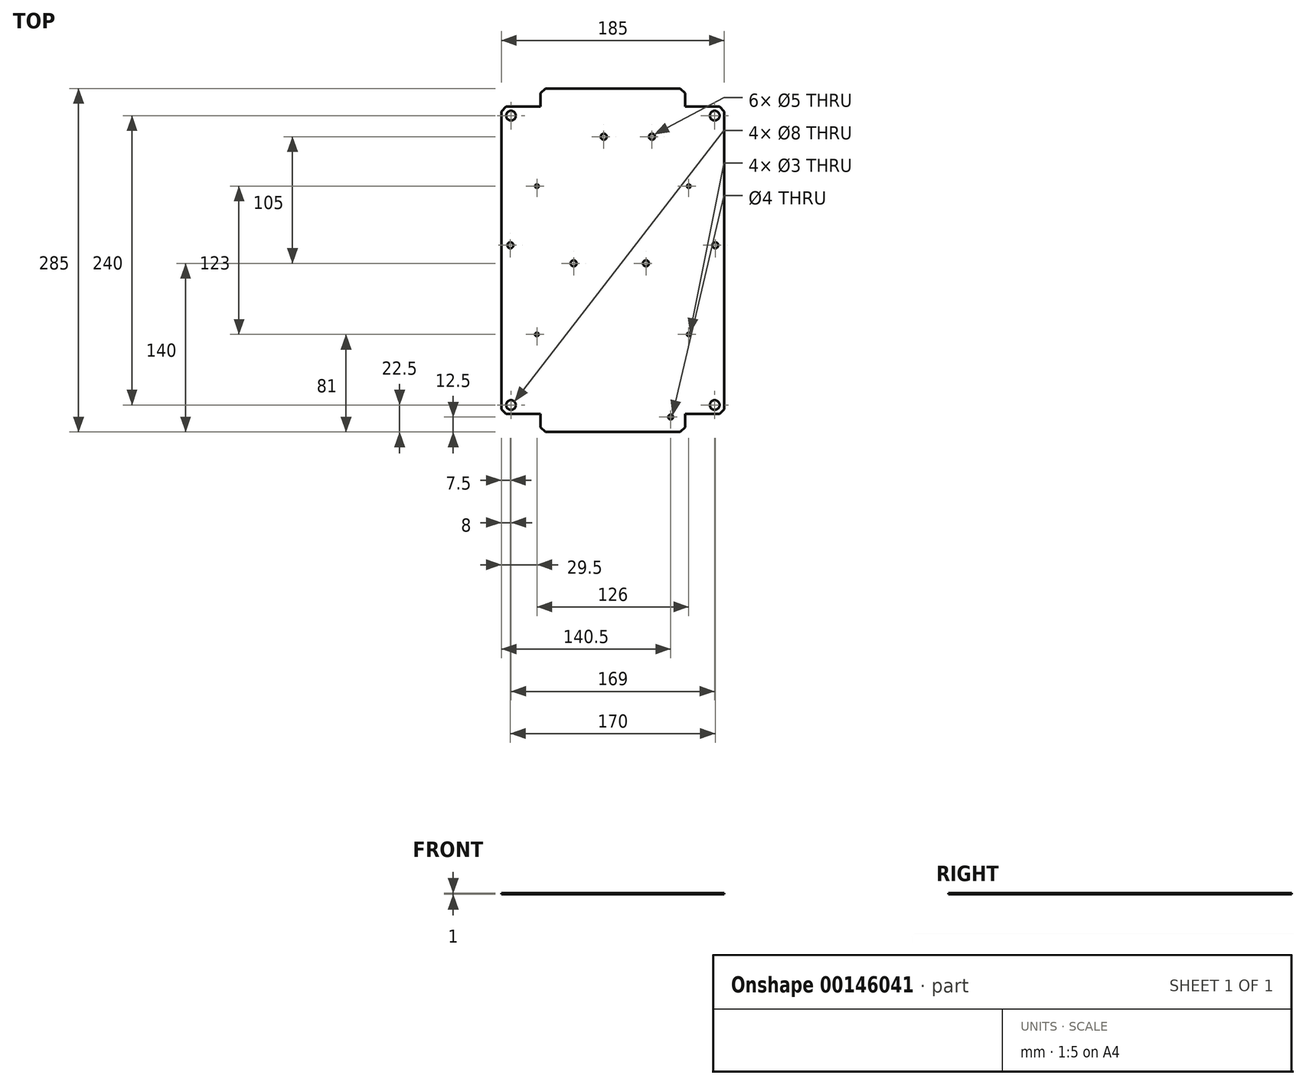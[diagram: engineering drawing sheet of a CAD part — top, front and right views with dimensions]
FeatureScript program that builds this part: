
annotation { "Feature Type Name" : "Feature", "Feature Type Description" : "" }
export const myFeature = defineFeature(function(context is Context, id is Id, definition is map)
    precondition{}
    {
        {
            var Q0;
            Q0=qCreatedBy(makeId("Top.planeOp"),FACE);
            var sketch = newSketch(context, id + "F0", { "sketchPlane" : qUnion([Q0])});
            skLineSegment(sketch, "E0", {"start": v(-92.5, 0) * mm, "end": v(-92.5, 127.5) * mm});
            skLineSegment(sketch, "E1", {"start": v(-92.5, 127.5) * mm, "end": v(-60, 127.5) * mm});
            skLineSegment(sketch, "E2", {"start": v(-60, 127.5) * mm, "end": v(-60, 142.5) * mm});
            skLineSegment(sketch, "E3", {"start": v(-60, 142.5) * mm, "end": v(0, 142.5) * mm});
            skCircle(sketch, "E4", {"center": v(-84.5, 120) * mm, "radius": 4 * mm});
            skCircle(sketch, "E5.MirrorC", {"center": v(84.5, 120) * mm, "radius": 4 * mm});
            skLineSegment(sketch, "E6.MirrorCS", {"start": v(60, 127.5) * mm, "end": v(60, 142.5) * mm});
            skLineSegment(sketch, "E7.MirrorCS", {"start": v(60, 142.5) * mm, "end": v(0, 142.5) * mm});
            skLineSegment(sketch, "E8.MirrorCS", {"start": v(92.5, 0) * mm, "end": v(92.5, 127.5) * mm});
            skLineSegment(sketch, "E9.MirrorCS", {"start": v(92.5, 127.5) * mm, "end": v(60, 127.5) * mm});
            skCircle(sketch, "E10.MirrorC", {"center": v(84.5, -120) * mm, "radius": 4 * mm});
            skCircle(sketch, "E11.MirrorC", {"center": v(-84.5, -120) * mm, "radius": 4 * mm});
            skLineSegment(sketch, "E12.MirrorCS", {"start": v(-60, -142.5) * mm, "end": v(0, -142.5) * mm});
            skLineSegment(sketch, "E13.MirrorCS", {"start": v(-60, -127.5) * mm, "end": v(-60, -142.5) * mm});
            skLineSegment(sketch, "E14.MirrorCS", {"start": v(-92.5, 0) * mm, "end": v(-92.5, -127.5) * mm});
            skLineSegment(sketch, "E15.MirrorCS", {"start": v(-92.5, -127.5) * mm, "end": v(-60, -127.5) * mm});
            skLineSegment(sketch, "E16.MirrorCS", {"start": v(60, -127.5) * mm, "end": v(60, -142.5) * mm});
            skLineSegment(sketch, "E17.MirrorCS", {"start": v(60, -142.5) * mm, "end": v(0, -142.5) * mm});
            skLineSegment(sketch, "E18.MirrorCS", {"start": v(92.5, -127.5) * mm, "end": v(60, -127.5) * mm});
            skLineSegment(sketch, "E19.MirrorCS", {"start": v(92.5, 0) * mm, "end": v(92.5, -127.5) * mm});
            skCircle(sketch, "E20", {"center": v(48, -130) * mm, "radius": 2 * mm});
            skCircle(sketch, "E21", {"center": v(-63, 61.5) * mm, "radius": 1.5 * mm});
            skCircle(sketch, "E22.MirrorC", {"center": v(63, 61.5) * mm, "radius": 1.5 * mm});
            skCircle(sketch, "E23.MirrorC", {"center": v(-63, -61.5) * mm, "radius": 1.5 * mm});
            skCircle(sketch, "E24.MirrorC", {"center": v(63, -61.5) * mm, "radius": 1.5 * mm});
            skCircle(sketch, "E25", {"center": v(32.5, 102.5) * mm, "radius": 2.5 * mm});
            skCircle(sketch, "E26", {"center": v(-7.5, 102.5) * mm, "radius": 2.5 * mm});
            skCircle(sketch, "E27", {"center": v(-32.5, -2.5) * mm, "radius": 2.5 * mm});
            skCircle(sketch, "E28", {"center": v(27.5, -2.5) * mm, "radius": 2.5 * mm});
            skCircle(sketch, "E29", {"center": v(-85, 12.5) * mm, "radius": 2.5 * mm});
            skCircle(sketch, "E30", {"center": v(85, 12.5) * mm, "radius": 2.5 * mm});
            skSolve(sketch);
        }
        {
            var Q0;
            Q0 = qSketchRegion(id + "F0", true);
            extrude(context, id + "F1", {"entities" : qUnion([Q0]), "endBound" : BoundingType.SYMMETRIC, "depth" : 1 * mm});
        }
        {
            var Q0;
            Q0=makeQuery(id+"F1.opExtrude","SWEPT_EDGE",EDGE,{"disambiguationData":[OSD([sQuery(id+"F0.wireOp",EDGE,"E0"),sQuery(id+"F0.wireOp",EDGE,"E1")])]});
            var Q1;
            Q1=makeQuery(id+"F1.opExtrude","SWEPT_EDGE",EDGE,{"disambiguationData":[OSD([sQuery(id+"F0.wireOp",EDGE,"E2"),sQuery(id+"F0.wireOp",EDGE,"E3")])]});
            var Q2;
            Q2=makeQuery(id+"F1.opExtrude","SWEPT_EDGE",EDGE,{"disambiguationData":[OSD([sQuery(id+"F0.wireOp",EDGE,"E6.MirrorCS"),sQuery(id+"F0.wireOp",EDGE,"E7.MirrorCS")])]});
            var Q3;
            Q3=makeQuery(id+"F1.opExtrude","SWEPT_EDGE",EDGE,{"disambiguationData":[OSD([sQuery(id+"F0.wireOp",EDGE,"E8.MirrorCS"),sQuery(id+"F0.wireOp",EDGE,"E9.MirrorCS")])]});
            var Q4;
            Q4=makeQuery(id+"F1.opExtrude","SWEPT_EDGE",EDGE,{"disambiguationData":[OSD([sQuery(id+"F0.wireOp",EDGE,"E18.MirrorCS"),sQuery(id+"F0.wireOp",EDGE,"E19.MirrorCS")])]});
            var Q5;
            Q5=makeQuery(id+"F1.opExtrude","SWEPT_EDGE",EDGE,{"disambiguationData":[OSD([sQuery(id+"F0.wireOp",EDGE,"E16.MirrorCS"),sQuery(id+"F0.wireOp",EDGE,"E17.MirrorCS")])]});
            var Q6;
            Q6=makeQuery(id+"F1.opExtrude","SWEPT_EDGE",EDGE,{"disambiguationData":[OSD([sQuery(id+"F0.wireOp",EDGE,"E12.MirrorCS"),sQuery(id+"F0.wireOp",EDGE,"E13.MirrorCS")])]});
            var Q7;
            Q7=makeQuery(id+"F1.opExtrude","SWEPT_EDGE",EDGE,{"disambiguationData":[OSD([sQuery(id+"F0.wireOp",EDGE,"E14.MirrorCS"),sQuery(id+"F0.wireOp",EDGE,"E15.MirrorCS")])]});
            chamfer(context, id + "F2", {"entities" : qUnion([Q0, Q1, Q2, Q3, Q4, Q5, Q6, Q7]), "width" : 4 * mm, "tangentPropagation" : true});
        }
    });
